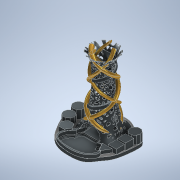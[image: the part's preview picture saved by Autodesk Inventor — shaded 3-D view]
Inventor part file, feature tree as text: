
AUTODESK INVENTOR PART (.ipt)
format: ipt  version: 2022 (Build 260153000, 153)  size: 9,089,024 bytes
history: native  units: mm
features: sketch x24, extrude x17, helix x5, plane x3, fillet x3, revolve x2, pattern_circular x2
ambient origin geometry x8: Origin, YZ Plane, XZ Plane, XY Plane, X Axis, Y Axis, Z Axis, Center Point
bodies: Solid1 (feature_tree)
feature tree (56):
  revolve  "Revolution1"  [1 undecoded]
  plane  "Work Plane1"
  extrude  "Extrusion4"  Depth=20.0mm
  extrude  "Extrusion2"  Depth=29.0mm
  pattern_circular  "Circular Pattern2"  Count=12  [1 undecoded]
  plane  "Work Plane3"
  extrude  "Extrusion3"  Depth=10.0mm
  pattern_circular  "Circular Pattern3"  Count=7  [1 undecoded]
  helix  "Coil1"  [1 undecoded]
  helix  "Coil2"  [1 undecoded]
  helix  "Coil3"  [1 undecoded]
  helix  "Coil4"  [1 undecoded]
  helix  "Coil5"  [1 undecoded]
  extrude  "Extrusion5"  Depth=20.0mm
  revolve  "Revolution2"  [1 undecoded]
  extrude  "Extrusion6"  Depth=30.0mm
  extrude  "Extrusion7"  Depth=15.0mm
  fillet  "Fillet1"  Radius=15.0mm
  fillet  "Fillet2"  Radius=30.0mm
  extrude  "Extrusion15"  Depth=45.0mm
  extrude  "Extrusion16"  Depth=13.0mm
  extrude  "Extrusion17"  Depth=39.0mm
  extrude  "Extrusion18"  Depth=11.0mm
  extrude  "Extrusion19"  Depth=10.0mm
  extrude  "Extrusion20"  Depth=11.0mm
  extrude  "Extrusion21"  Depth=9.0mm
  extrude  "Extrusion22"  Depth=3.0mm TaperAngle=0.0deg
  extrude  "Extrusion23"  Depth=60.0mm
  extrude  "Extrusion25"  Depth=46.0mm
  fillet  "Fillet3"  [1 undecoded]
  extrude  "Extrusion26"  Depth=70.0mm
  sketch  "Sketch1"  dims[d11=60.0mm d12=40.0mm]
  sketch  "Sketch3"  dims[d13=20.0mm d14=20.0mm]
  plane  "Work Plane2"
  sketch  "Sketch4"  dims[d15=20.0mm d16=29.0mm d17=120.0mm]
  sketch  "Sketch5"  dims[d18=50.0mm d19=10.0mm]
  sketch  "Sketch7"  dims[d20=209.0mm]
  sketch  "Sketch8"  dims[d26=2.0mm]
  sketch  "Sketch9"  dims[d27=2.0mm]
  sketch  "Sketch10"  dims[d28=2.0mm]
  sketch  "Sketch11"  dims[d29=2.0mm]
  sketch  "Sketch13"  dims[d30=2.0mm]
  sketch  "Sketch16"  dims[d31=90.0deg d32=70.0mm d38=77.75mm d39=0.0mm d40=40.0mm d41=360.0deg d43=70.0mm d44=77.75mm d45=0.0mm d46=40.0mm d47=360.0deg]
  sketch  "Sketch17"  dims[d49=20.0mm d50=20.0mm]
  sketch  "Sketch19"  dims[d51=20.0mm d52=20.0mm]
  sketch  "Sketch20"  dims[d53=40.0mm d54=30.0mm]
  sketch  "Sketch21"  dims[d55=30.0mm d56=15.0mm d57=15.0mm d58=30.0mm]
  sketch  "Sketch22"  dims[d59=77.75mm d60=0.0mm d61=45.0mm]
  sketch  "Sketch23"  dims[d62=35.0mm]
  sketch  "Sketch24"  dims[d63=70.0mm d64=150.0mm d65=10.0mm d66=-0.567232mm d67=90.0deg d68=90.0deg d69=90.0deg d70=90.0deg d71=13.0mm]
  sketch  "Sketch25"  dims[d72=10.0mm d73=39.0mm]
  sketch  "Sketch26"  dims[d74=150.0mm d75=210.0mm d76=10.0mm d77=-0.645772mm d78=90.0deg d79=90.0deg d80=90.0deg d81=90.0deg d82=11.0mm]
  sketch  "Sketch27"  dims[d83=39.0mm d84=10.0mm]
  sketch  "Sketch28"  dims[d85=170.0mm d86=210.0mm d87=10.0mm d88=-0.645772mm d89=90.0deg d90=90.0deg d91=90.0deg d92=90.0deg d93=11.0mm]
  sketch  "Sketch30"  dims[d94=200.0mm d95=210.0mm d96=10.0mm d97=-0.645772mm d98=90.0deg d99=90.0deg d100=90.0deg d101=90.0deg d102=9.0mm]
  sketch  "Sketch31"  dims[d103=170.0mm d104=210.0mm d105=10.0mm d106=-0.645772mm d107=90.0deg d108=90.0deg d109=90.0deg d110=90.0deg d125=3.0mm d126=0.0mm d128=60.0mm d129=46.0mm d130=270.0deg d131=70.0mm d132=35.0mm d133=54.0mm d134=0.0mm d136=54.0mm d137=0.0mm d138=73.12351mm d139=5.0mm d140=5.0mm d141=30.0mm d165=30.0mm d166=25.0mm d167=25.0mm d168=25.0mm d169=25.0mm d170=30.0mm d171=30.0mm d172=30.0mm d173=65.0mm d174=40.0mm d177=65.0mm d180=130.0mm d181=110.0mm d182=60.0mm d183=90.0mm d184=110.0mm d186=5.0mm d187=10.0mm d188=0.0mm d190=5.0mm d191=0.0mm d192=10.0mm d193=0.0mm d194=15.0mm d195=0.0mm d196=0.2mm d197=0.0mm d198=5.0mm d199=0.0mm d200=10.0mm d201=0.0mm d202=15.0mm d203=0.0mm d204=10.0mm d205=0.0mm d210=7.0mm d211=0.0mm d212=3.6mm d213=10.0mm d214=0.0mm d135=0.0mm]
note: 10 required parameter values undecoded (feature->parameter linkage not recoverable at this tier; creation-order binding heuristic only, values carry confidence <= 0.55)